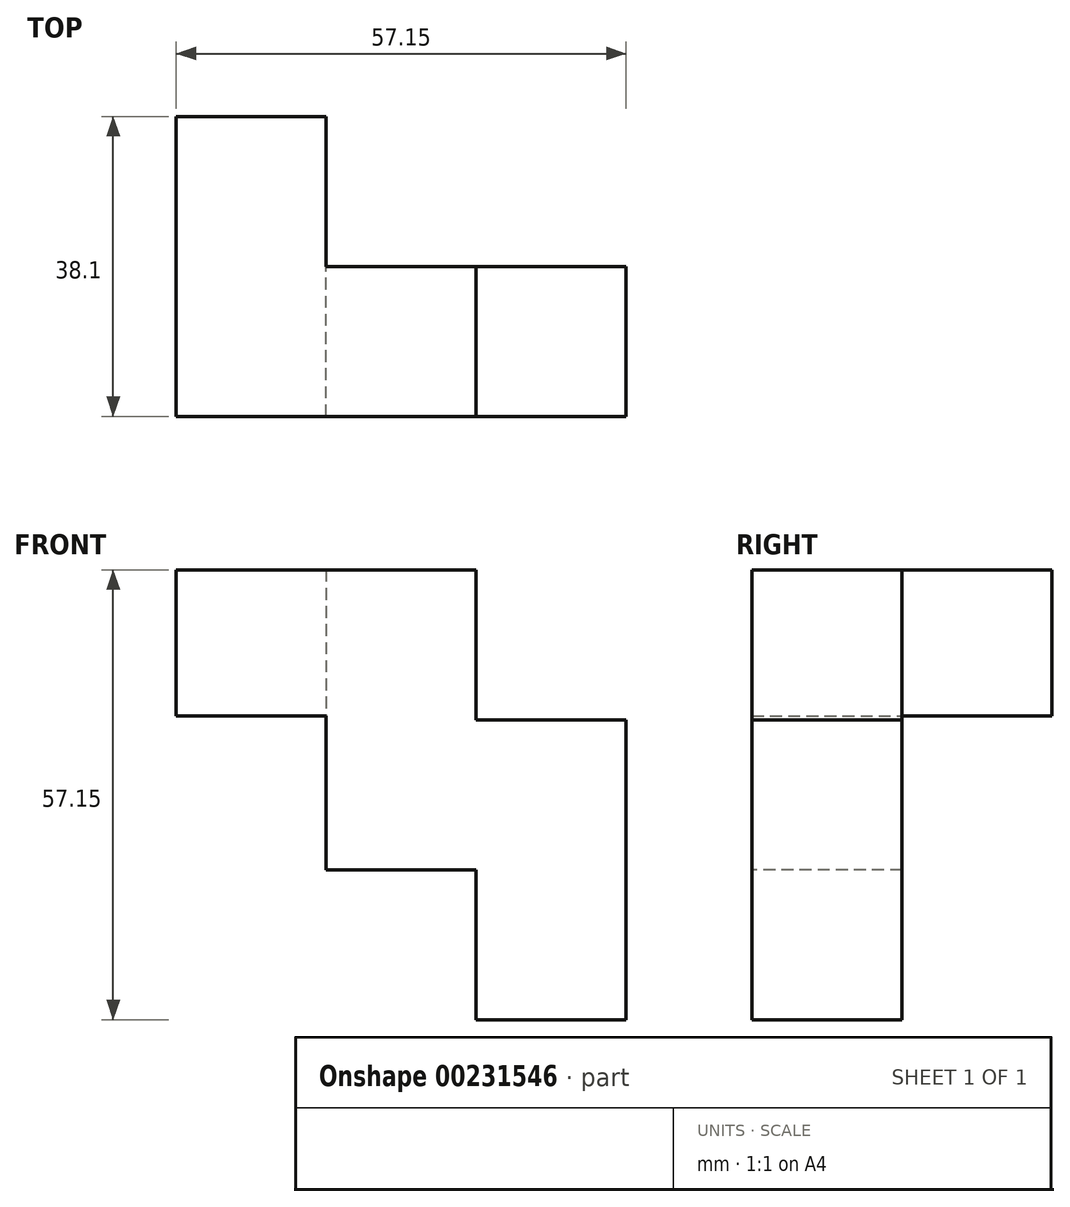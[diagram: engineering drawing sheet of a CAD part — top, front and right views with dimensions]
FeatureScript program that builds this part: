
annotation { "Feature Type Name" : "Feature", "Feature Type Description" : "" }
export const myFeature = defineFeature(function(context is Context, id is Id, definition is map)
    precondition{}
    {
        {
            var Q0;
            Q0=qCreatedBy(makeId("Front.planeOp"),FACE);
            var sketch = newSketch(context, id + "F0", { "sketchPlane" : qUnion([Q0])});
            skLineSegment(sketch, "E0.bottom", {"start": v(-53.21, 18.58) * mm, "end": v(-34.16, 18.58) * mm});
            skLineSegment(sketch, "E0.top", {"start": v(-53.21, -19.52) * mm, "end": v(-34.16, -19.52) * mm});
            skLineSegment(sketch, "E0.left", {"start": v(-53.21, 18.58) * mm, "end": v(-53.21, -19.52) * mm});
            skLineSegment(sketch, "E0.right", {"start": v(-34.16, 18.58) * mm, "end": v(-34.16, -19.52) * mm});
            skLineSegment(sketch, "E1.bottom", {"start": v(-34.16, -0.47) * mm, "end": v(-15.11, -0.47) * mm});
            skLineSegment(sketch, "E1.top", {"start": v(-34.16, -38.57) * mm, "end": v(-15.11, -38.57) * mm});
            skLineSegment(sketch, "E1.left", {"start": v(-34.16, -0.47) * mm, "end": v(-34.16, -38.57) * mm});
            skLineSegment(sketch, "E1.right", {"start": v(-15.11, -0.47) * mm, "end": v(-15.11, -38.57) * mm});
            skSolve(sketch);
        }
        {
            var Q0;
            Q0=makeQuery(id+"F0.imprint","IMPRINT",FACE,{"disambiguationData":[TD([[makeQuery(id+"F0.imprint","IMPRINT",EDGE,{"derivedFrom":sQuery(id+"F0.wireOp",EDGE,"E0.bottom")}),-1.0]])]});
            var Q1;
            {var subQ3=sQuery(id+"F0.wireOp",EDGE,"E1.bottom");Q1=makeQuery(id+"F0.imprint","IMPRINT",FACE,{"disambiguationData":[TD([[makeQuery(id+"F0.imprint","IMPRINT",EDGE,{"derivedFrom":subQ3}),-1.0]])]});}
            extrude(context, id + "F1", {"entities" : qUnion([Q0, Q1]), "oppositeDirection" : true, "depth" : 19.05 * mm});
        }
        {
            var Q0;
            Q0=makeQuery(id+"F1.opExtrude","SWEPT_FACE",FACE,{"disambiguationData":[OSD([sQuery(id+"F0.wireOp",EDGE,"E0.left")])]});
            var sketch = newSketch(context, id + "F2", { "sketchPlane" : qUnion([Q0])});
            skLineSegment(sketch, "E2.bottom", {"start": v(0, 18.58) * mm, "end": v(-38.1, 18.58) * mm});
            skLineSegment(sketch, "E2.top", {"start": v(0, 0) * mm, "end": v(-38.1, 0) * mm});
            skLineSegment(sketch, "E2.left", {"start": v(0, 18.58) * mm, "end": v(0, 0) * mm});
            skLineSegment(sketch, "E2.right", {"start": v(-38.1, 18.58) * mm, "end": v(-38.1, 0) * mm});
            skSolve(sketch);
        }
        {
            var Q0;
            {var subQ0=sQuery(id+"F2.wireOp",EDGE,"E2.left");Q0=makeQuery(id+"F2.imprint","IMPRINT",FACE,{"disambiguationData":[TD([[makeQuery(id+"F2.imprint","IMPRINT",EDGE,{"derivedFrom":subQ0}),-1.0]])]});}
            var Q1;
            {var subQ3=sQuery(id+"F2.wireOp",EDGE,"E2.right");Q1=makeQuery(id+"F2.imprint","IMPRINT",FACE,{"disambiguationData":[TD([[makeQuery(id+"F2.imprint","IMPRINT",EDGE,{"derivedFrom":subQ3}),1.0]])]});}
            extrude(context, id + "F3", {"entities" : qUnion([Q0, Q1]), "operationType" : NewBodyOperationType.ADD, "depth" : 19.05 * mm});
        }
    });
